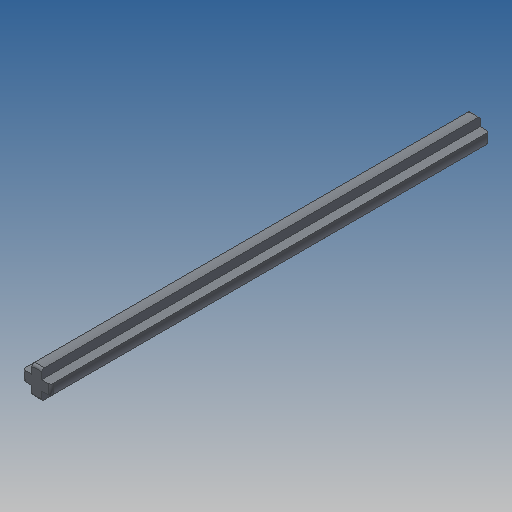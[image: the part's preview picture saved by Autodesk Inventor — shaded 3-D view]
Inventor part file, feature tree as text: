
AUTODESK INVENTOR PART (.ipt)
format: ipt  version: 2022.2 (Build 262287000, 287)  size: 145,408 bytes
history: native  units: in
note: dims shown in document units (in); Inventor stores cm internally (conversion verified against a paired STEP export)
features: extrude x1, fillet x1, sketch x1
ambient origin geometry x8: Origin, YZ Plane, XZ Plane, XY Plane, X Axis, Y Axis, Z Axis, Center Point
bodies: Solid1 (feature_tree)
feature tree (3):
  extrude  "Extrusion1"  Depth=0.0157in
  fillet  "Fillet1"  Radius=2.8346in
  sketch  "Sketch1"  dims[d0=0.189in d1=0.063in d2=2.8346in d3=0.0in d4=0.0157in d5=0.0in d6=0.0in]
